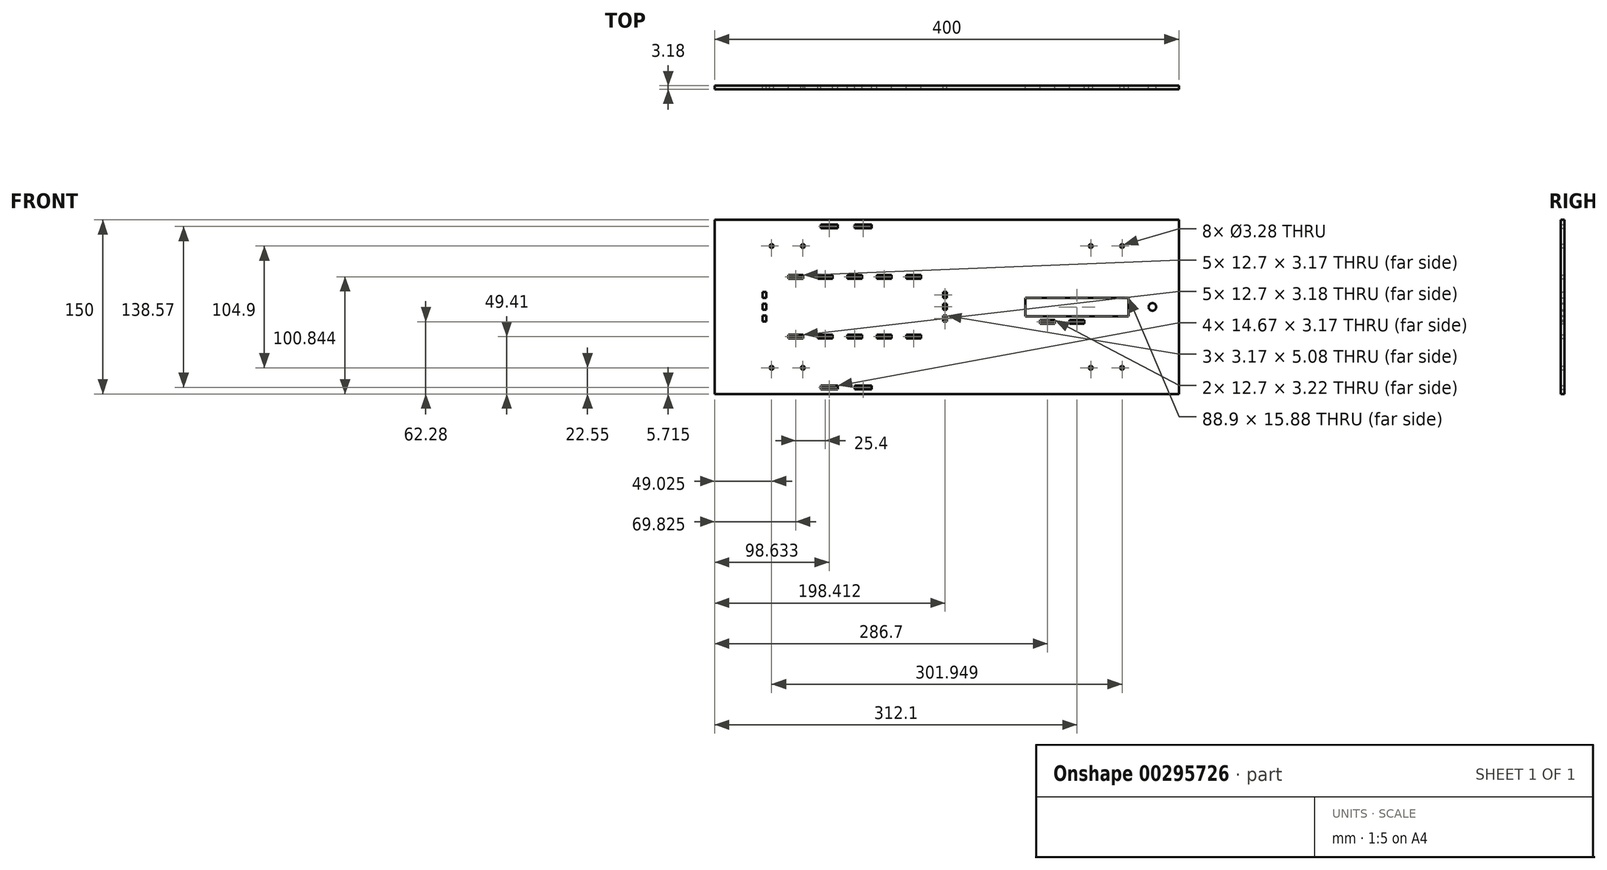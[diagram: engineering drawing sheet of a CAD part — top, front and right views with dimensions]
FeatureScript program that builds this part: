
annotation { "Feature Type Name" : "Feature", "Feature Type Description" : "" }
export const myFeature = defineFeature(function(context is Context, id is Id, definition is map)
    precondition{}
    {
        {
            var Q0;
            Q0=qCreatedBy(makeId("Front.planeOp"),FACE);
            var sketch = newSketch(context, id + "F0", { "sketchPlane" : qUnion([Q0])});
            skLineSegment(sketch, "E0.bottom", {"start": v(200, -75) * mm, "end": v(-200, -75) * mm});
            skLineSegment(sketch, "E0.top", {"start": v(200, 75) * mm, "end": v(-200, 75) * mm});
            skLineSegment(sketch, "E0.left", {"start": v(200, -75) * mm, "end": v(200, 75) * mm});
            skLineSegment(sketch, "E0.right", {"start": v(-200, -75) * mm, "end": v(-200, 75) * mm});
            skPoint(sketch, "E0.middle", {"position": v(0, 0) * mm});
            skCircle(sketch, "E1", {"center": v(-137.5, 52.45) * mm, "radius": 4 * mm, "construction": true});
            skLineSegment(sketch, "E2", {"start": v(-137.5, 52.45) * mm, "end": v(-133.5, 52.45) * mm, "construction": true});
            skLineSegment(sketch, "E3", {"start": v(-137.5, 52.45) * mm, "end": v(-137.5, 56.45) * mm, "construction": true});
            skCircle(sketch, "E4", {"center": v(-124.03, 52.45) * mm, "radius": 1.64 * mm});
            skCircle(sketch, "E5.MirrorC", {"center": v(-150.97, 52.45) * mm, "radius": 1.64 * mm});
            skCircle(sketch, "E6", {"center": v(-137.5, -52.45) * mm, "radius": 4 * mm, "construction": true});
            skLineSegment(sketch, "E7", {"start": v(-137.5, -52.45) * mm, "end": v(-133.5, -52.45) * mm, "construction": true});
            skLineSegment(sketch, "E8", {"start": v(-137.5, -52.45) * mm, "end": v(-137.5, -48.45) * mm, "construction": true});
            skCircle(sketch, "E9", {"center": v(-124.03, -52.45) * mm, "radius": 1.64 * mm});
            skCircle(sketch, "E10.MirrorC", {"center": v(-150.97, -52.45) * mm, "radius": 1.64 * mm});
            skCircle(sketch, "E11", {"center": v(137.5, -52.45) * mm, "radius": 4 * mm, "construction": true});
            skLineSegment(sketch, "E12", {"start": v(137.5, -52.45) * mm, "end": v(141.5, -52.45) * mm, "construction": true});
            skLineSegment(sketch, "E13", {"start": v(137.5, -52.45) * mm, "end": v(137.5, -48.45) * mm, "construction": true});
            skCircle(sketch, "E14", {"center": v(150.97, -52.45) * mm, "radius": 1.64 * mm});
            skCircle(sketch, "E15.MirrorC", {"center": v(124.03, -52.45) * mm, "radius": 1.64 * mm});
            skCircle(sketch, "E16", {"center": v(137.5, 52.45) * mm, "radius": 4 * mm, "construction": true});
            skLineSegment(sketch, "E17", {"start": v(137.5, 52.45) * mm, "end": v(141.5, 52.45) * mm, "construction": true});
            skLineSegment(sketch, "E18", {"start": v(137.5, 52.45) * mm, "end": v(137.5, 56.45) * mm, "construction": true});
            skCircle(sketch, "E19", {"center": v(150.97, 52.45) * mm, "radius": 1.64 * mm});
            skCircle(sketch, "E20.MirrorC", {"center": v(124.03, 52.45) * mm, "radius": 1.64 * mm});
            skLineSegment(sketch, "E21.bottom", {"start": v(-94.03, -70.87) * mm, "end": v(-108.7, -70.87) * mm});
            skLineSegment(sketch, "E21.top", {"start": v(-94.03, -67.7) * mm, "end": v(-108.7, -67.7) * mm});
            skLineSegment(sketch, "E21.left", {"start": v(-94.03, -70.87) * mm, "end": v(-94.03, -67.7) * mm});
            skLineSegment(sketch, "E21.right", {"start": v(-108.7, -70.87) * mm, "end": v(-108.7, -67.7) * mm});
            skPoint(sketch, "E21.middle", {"position": v(-101.37, -69.28) * mm});
            skLineSegment(sketch, "E22.bottom", {"start": v(-64.7, -70.87) * mm, "end": v(-79.37, -70.87) * mm});
            skLineSegment(sketch, "E22.top", {"start": v(-64.7, -67.7) * mm, "end": v(-79.37, -67.7) * mm});
            skLineSegment(sketch, "E22.left", {"start": v(-64.7, -70.87) * mm, "end": v(-64.7, -67.7) * mm});
            skLineSegment(sketch, "E22.right", {"start": v(-79.37, -70.87) * mm, "end": v(-79.37, -67.7) * mm});
            skPoint(sketch, "E22.middle", {"position": v(-72.03, -69.28) * mm});
            skLineSegment(sketch, "E23.bottom", {"start": v(-99.4, -81.35) * mm, "end": v(-175.6, -81.35) * mm, "construction": true});
            skLineSegment(sketch, "E23.top", {"start": v(-99.4, -75) * mm, "end": v(-175.6, -75) * mm, "construction": true});
            skLineSegment(sketch, "E23.left", {"start": v(-99.4, -81.35) * mm, "end": v(-99.4, -75) * mm, "construction": true});
            skLineSegment(sketch, "E23.right", {"start": v(-175.6, -81.35) * mm, "end": v(-175.6, -75) * mm, "construction": true});
            skPoint(sketch, "E23.middle", {"position": v(-137.5, -78.17) * mm});
            skPoint(sketch, "E23.middle.positionSnap0", {"position": v(-137.5, -50.45) * mm});
            skPoint(sketch, "E23.centerSnap0", {"position": v(-137.5, -50.45) * mm});
            skLineSegment(sketch, "E24.bottom", {"start": v(-99.4, -75) * mm, "end": v(-74, -75) * mm, "construction": true});
            skLineSegment(sketch, "E24.top", {"start": v(-99.4, -81.35) * mm, "end": v(-74, -81.35) * mm, "construction": true});
            skLineSegment(sketch, "E24.left", {"start": v(-99.4, -75) * mm, "end": v(-99.4, -81.35) * mm, "construction": true});
            skLineSegment(sketch, "E24.right", {"start": v(-74, -75) * mm, "end": v(-74, -81.35) * mm, "construction": true});
            skLineSegment(sketch, "E25", {"start": v(-94.03, -67.7) * mm, "end": v(-79.37, -70.87) * mm, "construction": true});
            skPoint(sketch, "E26", {"position": v(-86.7, -69.28) * mm});
            skPoint(sketch, "E27", {"position": v(-86.7, -75) * mm});
            skLineSegment(sketch, "E28", {"start": v(-86.7, -75) * mm, "end": v(-86.7, -81.35) * mm, "construction": true});
            skLineSegment(sketch, "E29.MirrorCS", {"start": v(-99.4, 75) * mm, "end": v(-175.6, 75) * mm, "construction": true});
            skLineSegment(sketch, "E30.MirrorCS", {"start": v(-99.4, 75) * mm, "end": v(-74, 75) * mm, "construction": true});
            skLineSegment(sketch, "E31.MirrorCS", {"start": v(-99.4, 81.35) * mm, "end": v(-175.6, 81.35) * mm, "construction": true});
            skLineSegment(sketch, "E32.MirrorCS", {"start": v(-175.6, 81.35) * mm, "end": v(-175.6, 75) * mm, "construction": true});
            skLineSegment(sketch, "E33.MirrorCS", {"start": v(-99.4, 81.35) * mm, "end": v(-74, 81.35) * mm, "construction": true});
            skLineSegment(sketch, "E34.MirrorCS", {"start": v(-99.4, 75) * mm, "end": v(-99.4, 81.35) * mm, "construction": true});
            skLineSegment(sketch, "E35.MirrorCS", {"start": v(-86.7, 75) * mm, "end": v(-86.7, 81.35) * mm, "construction": true});
            skLineSegment(sketch, "E36.MirrorCS", {"start": v(-74, 75) * mm, "end": v(-74, 81.35) * mm, "construction": true});
            skLineSegment(sketch, "E37.MirrorCS", {"start": v(-64.7, 70.87) * mm, "end": v(-79.37, 70.87) * mm});
            skLineSegment(sketch, "E38.MirrorCS", {"start": v(-79.37, 70.87) * mm, "end": v(-79.37, 67.7) * mm});
            skLineSegment(sketch, "E39.MirrorCS", {"start": v(-64.7, 67.7) * mm, "end": v(-79.37, 67.7) * mm});
            skLineSegment(sketch, "E40.MirrorCS", {"start": v(-64.7, 70.87) * mm, "end": v(-64.7, 67.7) * mm});
            skLineSegment(sketch, "E41.MirrorCS", {"start": v(-94.03, 70.87) * mm, "end": v(-94.03, 67.7) * mm});
            skLineSegment(sketch, "E42.MirrorCS", {"start": v(-94.03, 67.7) * mm, "end": v(-108.7, 67.7) * mm});
            skLineSegment(sketch, "E43.MirrorCS", {"start": v(-108.7, 70.87) * mm, "end": v(-108.7, 67.7) * mm});
            skLineSegment(sketch, "E44.MirrorCS", {"start": v(-94.03, 70.87) * mm, "end": v(-108.7, 70.87) * mm});
            skLineSegment(sketch, "E45.MirrorCS", {"start": v(-94.03, 67.7) * mm, "end": v(-79.37, 70.87) * mm, "construction": true});
            skPoint(sketch, "E46.middle", {"position": v(-79.38, 0.13) * mm});
            skLineSegment(sketch, "E47.top", {"start": v(-3.18, -12.57) * mm, "end": v(-3.18, -7.5) * mm});
            skLineSegment(sketch, "E47.left", {"start": v(0, -12.57) * mm, "end": v(-3.18, -12.57) * mm});
            skLineSegment(sketch, "E47.right", {"start": v(0, -7.5) * mm, "end": v(-3.18, -7.5) * mm});
            skLineSegment(sketch, "E48.left", {"start": v(-3.18, -7.5) * mm, "end": v(0, -7.5) * mm});
            skLineSegment(sketch, "E48.right", {"start": v(-3.18, -2.41) * mm, "end": v(0, -2.41) * mm});
            skLineSegment(sketch, "E49.top", {"start": v(-3.18, -2.41) * mm, "end": v(-3.18, 2.67) * mm});
            skLineSegment(sketch, "E49.left", {"start": v(0, -2.41) * mm, "end": v(-3.18, -2.41) * mm});
            skLineSegment(sketch, "E49.right", {"start": v(0, 2.67) * mm, "end": v(-3.18, 2.67) * mm});
            skLineSegment(sketch, "E50.left", {"start": v(-3.18, 2.67) * mm, "end": v(0, 2.67) * mm});
            skLineSegment(sketch, "E50.right", {"start": v(-3.18, 7.75) * mm, "end": v(0, 7.75) * mm});
            skLineSegment(sketch, "E51.top", {"start": v(-3.18, 12.83) * mm, "end": v(-3.18, 7.75) * mm});
            skLineSegment(sketch, "E51.left", {"start": v(0, 12.83) * mm, "end": v(-3.18, 12.83) * mm});
            skLineSegment(sketch, "E51.right", {"start": v(0, 7.75) * mm, "end": v(-3.18, 7.75) * mm});
            skLineSegment(sketch, "E52.MirrorCS", {"start": v(-158.75, -12.57) * mm, "end": v(-155.58, -12.57) * mm});
            skLineSegment(sketch, "E53.MirrorCS", {"start": v(-155.58, -12.57) * mm, "end": v(-155.58, -7.5) * mm});
            skLineSegment(sketch, "E54.MirrorCS", {"start": v(-158.75, -7.5) * mm, "end": v(-155.58, -7.5) * mm});
            skLineSegment(sketch, "E55.MirrorCS", {"start": v(-155.58, -2.41) * mm, "end": v(-158.75, -2.41) * mm});
            skLineSegment(sketch, "E56.MirrorCS", {"start": v(-155.58, -2.41) * mm, "end": v(-155.58, 2.67) * mm});
            skLineSegment(sketch, "E57.MirrorCS", {"start": v(-158.75, 2.67) * mm, "end": v(-155.58, 2.67) * mm});
            skLineSegment(sketch, "E58.MirrorCS", {"start": v(-155.58, 7.75) * mm, "end": v(-158.75, 7.75) * mm});
            skLineSegment(sketch, "E59.MirrorCS", {"start": v(-155.58, 12.83) * mm, "end": v(-155.58, 7.75) * mm});
            skLineSegment(sketch, "E60.MirrorCS", {"start": v(-158.75, 12.83) * mm, "end": v(-155.58, 12.83) * mm});
            skLineSegment(sketch, "E61.bottom", {"start": v(-73.03, 24.26) * mm, "end": v(-73.03, 27.43) * mm});
            skLineSegment(sketch, "E61.top", {"start": v(-85.73, 24.26) * mm, "end": v(-85.73, 27.43) * mm});
            skLineSegment(sketch, "E61.left", {"start": v(-73.03, 24.26) * mm, "end": v(-85.73, 24.26) * mm});
            skLineSegment(sketch, "E62.bottom", {"start": v(-85.73, 27.43) * mm, "end": v(-85.73, 24.26) * mm});
            skLineSegment(sketch, "E62.top", {"start": v(-98.43, 27.43) * mm, "end": v(-98.43, 24.26) * mm});
            skLineSegment(sketch, "E63.bottom", {"start": v(-98.43, 24.26) * mm, "end": v(-98.43, 27.43) * mm});
            skLineSegment(sketch, "E63.top", {"start": v(-111.13, 24.26) * mm, "end": v(-111.13, 27.43) * mm});
            skLineSegment(sketch, "E63.left", {"start": v(-98.43, 24.26) * mm, "end": v(-111.13, 24.26) * mm});
            skLineSegment(sketch, "E64.bottom", {"start": v(-111.13, 27.43) * mm, "end": v(-111.13, 24.26) * mm});
            skLineSegment(sketch, "E64.top", {"start": v(-123.83, 27.43) * mm, "end": v(-123.83, 24.26) * mm});
            skLineSegment(sketch, "E65.bottom", {"start": v(-123.83, 24.26) * mm, "end": v(-123.83, 27.43) * mm});
            skLineSegment(sketch, "E65.top", {"start": v(-136.53, 24.26) * mm, "end": v(-136.53, 27.43) * mm});
            skLineSegment(sketch, "E65.left", {"start": v(-123.83, 24.26) * mm, "end": v(-136.53, 24.26) * mm});
            skLineSegment(sketch, "E66.MirrorCS", {"start": v(-60.33, 27.43) * mm, "end": v(-60.33, 24.26) * mm});
            skLineSegment(sketch, "E67.MirrorCS", {"start": v(-34.93, 24.26) * mm, "end": v(-34.93, 27.43) * mm});
            skLineSegment(sketch, "E68.MirrorCS", {"start": v(-47.63, 27.43) * mm, "end": v(-47.63, 24.26) * mm});
            skLineSegment(sketch, "E69.MirrorCS", {"start": v(-34.93, 27.43) * mm, "end": v(-34.93, 24.26) * mm});
            skLineSegment(sketch, "E70.MirrorCS", {"start": v(-47.63, 24.26) * mm, "end": v(-47.63, 27.43) * mm});
            skLineSegment(sketch, "E71.MirrorCS", {"start": v(-60.33, 24.26) * mm, "end": v(-60.33, 27.43) * mm});
            skLineSegment(sketch, "E72.MirrorCS", {"start": v(-22.22, 24.26) * mm, "end": v(-22.22, 27.43) * mm});
            skLineSegment(sketch, "E73.MirrorCS", {"start": v(-34.93, 24.26) * mm, "end": v(-22.22, 24.26) * mm});
            skLineSegment(sketch, "E74.MirrorCS", {"start": v(-60.33, 24.26) * mm, "end": v(-47.63, 24.26) * mm});
            skLineSegment(sketch, "E75.MirrorCS", {"start": v(-98.43, -27.18) * mm, "end": v(-98.43, -24) * mm});
            skLineSegment(sketch, "E76.MirrorCS", {"start": v(-60.33, -24) * mm, "end": v(-60.33, -27.18) * mm});
            skLineSegment(sketch, "E77.MirrorCS", {"start": v(-47.63, -27.18) * mm, "end": v(-47.63, -24) * mm});
            skLineSegment(sketch, "E78.MirrorCS", {"start": v(-85.73, -24) * mm, "end": v(-85.73, -27.18) * mm});
            skLineSegment(sketch, "E79.MirrorCS", {"start": v(-123.83, -27.18) * mm, "end": v(-123.83, -24) * mm});
            skLineSegment(sketch, "E80.MirrorCS", {"start": v(-111.13, -24) * mm, "end": v(-111.13, -27.18) * mm});
            skLineSegment(sketch, "E81.MirrorCS", {"start": v(-34.93, -27.18) * mm, "end": v(-34.93, -24) * mm});
            skLineSegment(sketch, "E82.MirrorCS", {"start": v(-123.83, -24) * mm, "end": v(-123.83, -27.18) * mm});
            skLineSegment(sketch, "E83.MirrorCS", {"start": v(-85.73, -27.18) * mm, "end": v(-85.73, -24) * mm});
            skLineSegment(sketch, "E84.MirrorCS", {"start": v(-34.93, -24) * mm, "end": v(-34.93, -27.18) * mm});
            skLineSegment(sketch, "E85.MirrorCS", {"start": v(-111.13, -27.18) * mm, "end": v(-111.13, -24) * mm});
            skLineSegment(sketch, "E86.MirrorCS", {"start": v(-47.63, -24) * mm, "end": v(-47.63, -27.18) * mm});
            skLineSegment(sketch, "E87.MirrorCS", {"start": v(-60.33, -27.18) * mm, "end": v(-60.33, -24) * mm});
            skLineSegment(sketch, "E88.MirrorCS", {"start": v(-98.43, -24) * mm, "end": v(-98.43, -27.18) * mm});
            skLineSegment(sketch, "E89.MirrorCS", {"start": v(-73.03, -24) * mm, "end": v(-73.03, -27.18) * mm});
            skLineSegment(sketch, "E90.MirrorCS", {"start": v(-136.53, -24) * mm, "end": v(-136.53, -27.18) * mm});
            skLineSegment(sketch, "E91.MirrorCS", {"start": v(-22.22, -24) * mm, "end": v(-22.22, -27.18) * mm});
            skLineSegment(sketch, "E92.MirrorCS", {"start": v(-73.03, -24) * mm, "end": v(-85.73, -24) * mm});
            skLineSegment(sketch, "E93.MirrorCS", {"start": v(-123.83, -24) * mm, "end": v(-136.53, -24) * mm});
            skLineSegment(sketch, "E94.MirrorCS", {"start": v(-60.33, -24) * mm, "end": v(-47.63, -24) * mm});
            skLineSegment(sketch, "E95.MirrorCS", {"start": v(-98.43, -24) * mm, "end": v(-111.13, -24) * mm});
            skLineSegment(sketch, "E96.MirrorCS", {"start": v(-34.93, -24) * mm, "end": v(-22.22, -24) * mm});
            skLineSegment(sketch, "E97", {"start": v(-158.75, 12.83) * mm, "end": v(-158.75, 7.75) * mm});
            skLineSegment(sketch, "E98", {"start": v(-158.75, 2.67) * mm, "end": v(-158.75, -2.41) * mm});
            skLineSegment(sketch, "E99", {"start": v(-158.75, -7.5) * mm, "end": v(-158.75, -12.57) * mm});
            skLineSegment(sketch, "E100", {"start": v(-136.53, 27.43) * mm, "end": v(-123.83, 27.43) * mm});
            skLineSegment(sketch, "E101", {"start": v(-111.13, 27.43) * mm, "end": v(-98.43, 27.43) * mm});
            skLineSegment(sketch, "E102", {"start": v(-85.73, 27.43) * mm, "end": v(-73.03, 27.43) * mm});
            skLineSegment(sketch, "E103", {"start": v(-60.33, 27.43) * mm, "end": v(-47.63, 27.43) * mm});
            skLineSegment(sketch, "E104", {"start": v(-34.93, 27.43) * mm, "end": v(-22.22, 27.43) * mm});
            skLineSegment(sketch, "E105", {"start": v(0, 12.83) * mm, "end": v(0, 7.75) * mm});
            skLineSegment(sketch, "E106", {"start": v(0, 2.67) * mm, "end": v(0, -2.41) * mm});
            skLineSegment(sketch, "E107", {"start": v(0, -7.5) * mm, "end": v(0, -12.57) * mm});
            skLineSegment(sketch, "E108", {"start": v(-22.22, -27.18) * mm, "end": v(-34.93, -27.18) * mm});
            skLineSegment(sketch, "E109", {"start": v(-47.63, -27.18) * mm, "end": v(-60.33, -27.18) * mm});
            skLineSegment(sketch, "E110", {"start": v(-73.03, -27.18) * mm, "end": v(-85.73, -27.18) * mm});
            skLineSegment(sketch, "E111", {"start": v(-98.43, -27.18) * mm, "end": v(-111.13, -27.18) * mm});
            skLineSegment(sketch, "E112", {"start": v(-123.83, -27.18) * mm, "end": v(-136.53, -27.18) * mm});
            skLineSegment(sketch, "E113", {"start": v(137.5, 52.45) * mm, "end": v(137.5, -52.45) * mm, "construction": true});
            skLineSegment(sketch, "E114", {"start": v(137.5, 0) * mm, "end": v(76.32, 0) * mm, "construction": true});
            skPoint(sketch, "E114.endSnap0", {"position": v(137.5, 0) * mm});
            skLineSegment(sketch, "E115.bottom", {"start": v(156.55, -7.94) * mm, "end": v(118.45, -7.94) * mm});
            skLineSegment(sketch, "E115.top", {"start": v(156.55, 7.94) * mm, "end": v(118.45, 7.94) * mm});
            skLineSegment(sketch, "E115.left", {"start": v(156.55, -7.94) * mm, "end": v(156.55, 7.94) * mm});
            skLineSegment(sketch, "E115.right", {"start": v(118.45, -7.94) * mm, "end": v(118.45, 7.94) * mm});
            skLineSegment(sketch, "E116", {"start": v(137.5, 0) * mm, "end": v(200, 0) * mm, "construction": true});
            skLineSegment(sketch, "E117.MirrorCS", {"start": v(80.35, -7.94) * mm, "end": v(118.45, -7.94) * mm});
            skLineSegment(sketch, "E118.MirrorCS", {"start": v(80.35, 7.94) * mm, "end": v(118.45, 7.94) * mm});
            skLineSegment(sketch, "E119.MirrorCS", {"start": v(80.35, -7.94) * mm, "end": v(80.35, 7.94) * mm});
            skLineSegment(sketch, "E120.MirrorCS", {"start": v(93.05, -11.11) * mm, "end": v(93.05, -14.33) * mm});
            skLineSegment(sketch, "E121.MirrorCS", {"start": v(105.75, -11.11) * mm, "end": v(105.75, -14.33) * mm});
            skLineSegment(sketch, "E122.MirrorCS", {"start": v(80.35, -11.11) * mm, "end": v(80.35, -14.33) * mm});
            skLineSegment(sketch, "E123.MirrorCS", {"start": v(93.05, -14.33) * mm, "end": v(80.35, -14.33) * mm});
            skLineSegment(sketch, "E124.MirrorCS", {"start": v(118.45, -14.33) * mm, "end": v(105.75, -14.33) * mm});
            skLineSegment(sketch, "E125.MirrorCS", {"start": v(93.05, -11.11) * mm, "end": v(80.35, -11.11) * mm});
            skLineSegment(sketch, "E126.MirrorCS", {"start": v(93.05, -14.33) * mm, "end": v(93.05, -11.11) * mm});
            skLineSegment(sketch, "E127.MirrorCS", {"start": v(118.45, -11.11) * mm, "end": v(105.75, -11.11) * mm});
            skLineSegment(sketch, "E128.MirrorCS", {"start": v(105.75, -14.33) * mm, "end": v(105.75, -11.11) * mm});
            skLineSegment(sketch, "E129.MirrorCS", {"start": v(118.45, -11.11) * mm, "end": v(118.45, -14.33) * mm});
            skLineSegment(sketch, "E130", {"start": v(67.65, 7.94) * mm, "end": v(67.65, -7.94) * mm});
            skLineSegment(sketch, "E131", {"start": v(67.65, 7.94) * mm, "end": v(80.35, 7.94) * mm});
            skLineSegment(sketch, "E132", {"start": v(67.65, -7.94) * mm, "end": v(80.35, -7.94) * mm});
            skCircle(sketch, "E133", {"center": v(177.14, 0) * mm, "radius": 3.3 * mm});
            skSolve(sketch);
        }
        {
            var Q0;
            Q0 = qSketchRegion(id + "F0", true);
            extrude(context, id + "F1", {"entities" : qUnion([Q0]), "depth" : 3.17 * mm});
        }
    });
